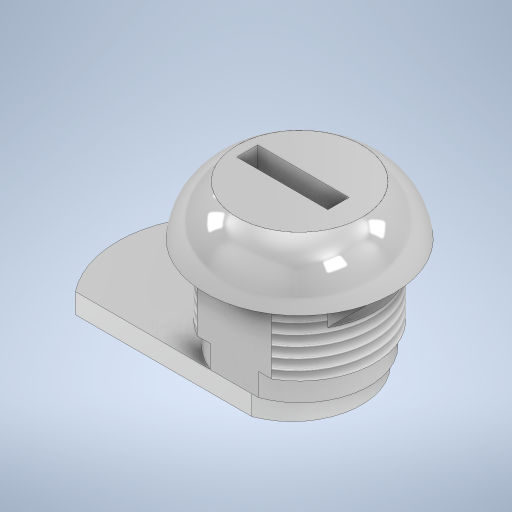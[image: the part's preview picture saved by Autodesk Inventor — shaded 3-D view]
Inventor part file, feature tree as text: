
AUTODESK INVENTOR PART (.ipt)
format: ipt  version: 2024 (Build 280153000, 153)  size: 413,184 bytes
history: native  units: in
note: dims shown in document units (in); Inventor stores cm internally (conversion verified against a paired STEP export)
features: sketch x7, extrude x6, projected_geometry x5, thread x1, fillet x1, plane x1, revolve x1
ambient origin geometry x8: Origin, YZ Plane, XZ Plane, XY Plane, X Axis, Y Axis, Z Axis, Center Point
bodies: Solid1 (feature_tree)
feature tree (22):
  extrude  "Extrusion1"  Depth=0.727in
  extrude  "Extrusion2"  Depth=0.632in
  thread  "Thread1"  [1 undecoded]
  extrude  "Extrusion3"  Depth=0.341in TaperAngle=0.0deg
  extrude  "Extrusion4"  Depth=0.11in TaperAngle=0.0deg
  extrude  "Extrusion5"  Depth=0.625in
  fillet  "Fillet1"  Radius=0.3in
  extrude  "Extrusion6"  Depth=0.097in TaperAngle=0.0deg
  plane  "Work Plane1"
  revolve  "Revolution1"  [1 undecoded]
  sketch  "Sketch1"  dims[d0=0.6319in d1=0.727in]
  sketch  "Sketch2"  dims[d2=0.316in d3=0.632in d4=0.126in d5=0.0in]
  projected_geometry  "Projected Loop1"
  sketch  "Sketch3"  dims[d6=0.215in d7=0.0in d8=0.341in d9=0.0in]
  projected_geometry  "Projected Loop2"
  sketch  "Sketch4"  dims[d10=0.673in d11=0.11in d12=0.0in]
  projected_geometry  "Projected Loop3"
  sketch  "Sketch6"  dims[d13=0.3125in d14=0.625in d15=0.3in]
  projected_geometry  "Projected Loop6"
  sketch  "Sketch7"  dims[d16=1.18in d17=0.097in d18=0.0in]
  sketch  "Sketch8"  dims[d19=0.435in d21=0.25in d22=0.05in d23=0.0in d24=0.03in d25=0.915in d27=0.155in d28=0.24in d29=0.0in d30=0.051in d31=0.4575in d32=90.0deg]
  projected_geometry  "Projected Loop7"
note: 2 required parameter values undecoded (feature->parameter linkage not recoverable at this tier; creation-order binding heuristic only, values carry confidence <= 0.55)